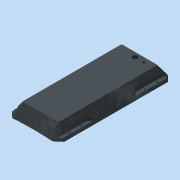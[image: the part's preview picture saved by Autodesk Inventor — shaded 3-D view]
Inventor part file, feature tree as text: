
AUTODESK INVENTOR PART (.ipt)
format: ipt  version: 2015 (Build 190159000, 159)  size: 491,008 bytes
history: native  units: in
note: dims shown in document units (in); Inventor stores cm internally (conversion verified against a paired STEP export)
features: sketch x14, extrude x13, projected_geometry x9, plane x5, fillet x5, loft x1, mirror x1
ambient origin geometry x8: Origin, YZ Plane, XZ Plane, XY Plane, X Axis, Y Axis, Z Axis, Center Point
bodies: Body1 (feature_tree)
feature tree (48):
  sketch  "Sketch1"  dims[d0=45.0deg d1=12.1574in]
  sketch  "Sketch5"  dims[d6=1.0in d7=1.0in]
  plane  "Work Plane1"
  loft  "Loft2"
  plane  "Work Plane2"
  extrude  "Extrusion1"  Depth=1.0in
  extrude  "Extrusion3"  Depth=1.0in
  plane  "Work Plane3"
  extrude  "Extrusion2"  Depth=1.0in
  plane  "Work Plane5"
  extrude  "Extrusion4"  Depth=0.125in
  extrude  "Extrusion5"  Depth=0.125in
  extrude  "Extrusion6"  Depth=0.125in
  extrude  "Extrusion7"  Depth=0.125in
  mirror  "Mirror1"
  extrude  "Extrusion8"  TaperAngle=0.0deg  [1 undecoded]
  extrude  "Extrusion10"  Depth=1.0in TaperAngle=0.0deg
  fillet  "Fillet1"  Radius=8.3074in
  extrude  "Extrusion11"  Depth=0.1875in TaperAngle=0.0deg
  extrude  "Extrusion12"  Depth=0.125in TaperAngle=0.0deg
  fillet  "Fillet3"  Radius=0.1875in
  extrude  "Extrusion13"  Depth=0.125in TaperAngle=0.0deg
  fillet  "Fillet4"  Radius=0.201in
  extrude  "Extrusion14"  Depth=1.5in
  fillet  "Fillet5"  Radius=0.125in
  fillet  "Fillet6"  Radius=0.0825in
  sketch  "Sketch3"  dims[d2=4.4in d3=1.0in]
  sketch  "Sketch4"  dims[d4=1.0in d5=1.0in]
  plane  "Work Plane4"
  sketch  "Sketch6"  dims[d21=0.125in d22=0.125in]
  sketch  "Sketch7"  dims[d23=0.125in d24=0.125in]
  sketch  "Sketch8"  dims[d25=0.125in d26=0.125in]
  sketch  "Sketch9"  dims[d27=0.125in d28=0.125in]
  projected_geometry  "Projected Loop1"
  sketch  "Sketch10"  dims[d29=0.0in d30=90.0deg d31=0.0in d32=90.0deg]
  projected_geometry  "Projected Loop2"
  sketch  "Sketch12"  dims[d33=-0.3125in d34=1.0in d35=0.0in d36=8.3074in]
  sketch  "Sketch13"  dims[d37=0.1875in d38=0.1875in d39=0.0in]
  sketch  "Sketch14"  dims[d41=1.362in d42=0.125in d43=0.0in d44=0.1875in]
  sketch  "Sketch15"  dims[d45=0.375in d47=0.125in d48=0.0in d49=0.201in]
  sketch  "Sketch16"  dims[d50=0.201in d51=1.5in d52=0.125in d53=0.0in d54=0.0825in d55=0.125in d56=0.0in d57=0.75in d58=0.0704in d59=1.0in d60=0.5in d61=0.1575in d62=0.1181in d63=0.0591in d64=0.0in d65=0.1875in d66=0.0in d69=1.0in d70=0.625in d71=0.125in d72=0.0in d73=0.125in d76=0.125in d77=0.0in d78=0.3189in d79=0.5512in d80=0.0133in d81=0.0in d82=0.0394in d83=1.0in d84=0.0054in d85=0.0in d86=0.0787in d87=0.3in d88=0.375in d89=0.0in d90=0.5in d91=0.0in d92=61.729in d93=0.0625in d94=0.0625in]
  projected_geometry  "Projected Loop3"
  projected_geometry  "Project Cut Edges1"
  projected_geometry  "Project Cut Edges2"
  projected_geometry  "Project Cut Edges3"
  projected_geometry  "Project Cut Edges5"
  projected_geometry  "Project Cut Edges6"
  projected_geometry  "Project Cut Edges7"
note: 1 required parameter value undecoded (feature->parameter linkage not recoverable at this tier; creation-order binding heuristic only, values carry confidence <= 0.55)
